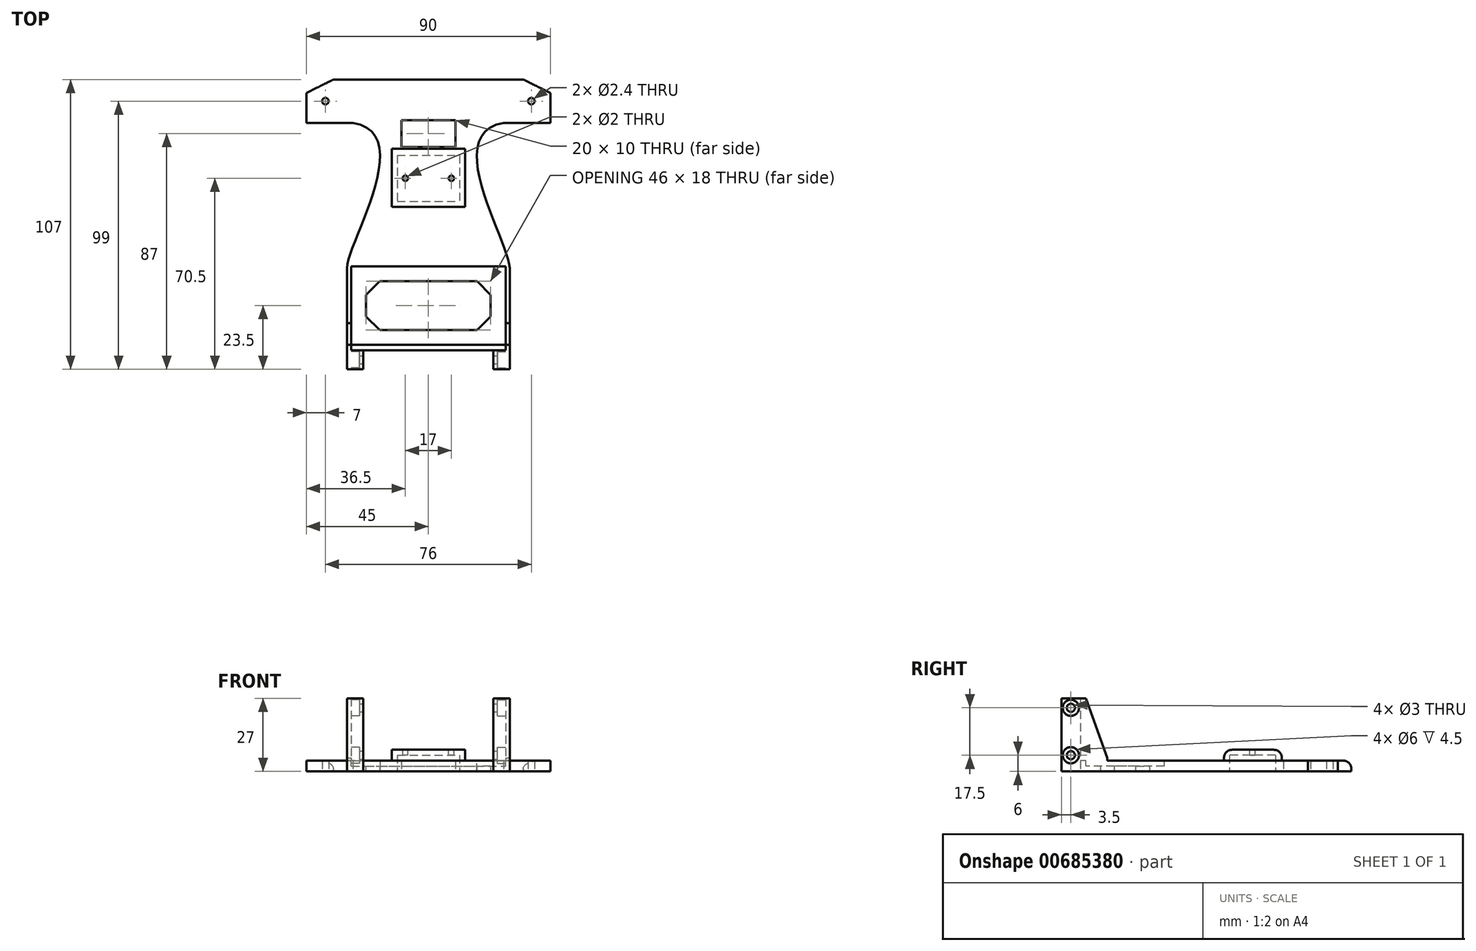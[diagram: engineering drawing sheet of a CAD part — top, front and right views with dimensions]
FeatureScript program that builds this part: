
annotation { "Feature Type Name" : "Feature", "Feature Type Description" : "" }
export const myFeature = defineFeature(function(context is Context, id is Id, definition is map)
    precondition{}
    {
        {
            var Q0;
            Q0=qCreatedBy(makeId("Top.planeOp"),FACE);
            var sketch = newSketch(context, id + "F0", { "sketchPlane" : qUnion([Q0])});
            skLineSegment(sketch, "E0", {"start": v(-45, 84) * mm, "end": v(-45, 68) * mm});
            skLineSegment(sketch, "E1", {"start": v(-45, 68) * mm, "end": v(-30, 68) * mm});
            skLineSegment(sketch, "E2", {"start": v(-30, 14.37) * mm, "end": v(-30, -16) * mm});
            skLineSegment(sketch, "E3", {"start": v(-30, -16) * mm, "end": v(0, -16) * mm});
            skLineSegment(sketch, "E4", {"start": v(-45, 84) * mm, "end": v(0, 84) * mm});
            skLineSegment(sketch, "E5.MirrorCS", {"start": v(45, 84) * mm, "end": v(0, 84) * mm});
            skLineSegment(sketch, "E6.MirrorCS", {"start": v(45, 84) * mm, "end": v(45, 68) * mm});
            skLineSegment(sketch, "E7.MirrorCS", {"start": v(45, 68) * mm, "end": v(30, 68) * mm});
            skLineSegment(sketch, "E8.MirrorCS", {"start": v(30, 14.37) * mm, "end": v(30, -16) * mm});
            skLineSegment(sketch, "E9.MirrorCS", {"start": v(30, -16) * mm, "end": v(0, -16) * mm});
            skCircle(sketch, "E10", {"center": v(-38, 76) * mm, "radius": 1.2 * mm});
            skCircle(sketch, "E11.MirrorC", {"center": v(38, 76) * mm, "radius": 1.2 * mm});
            skLineSegment(sketch, "E12", {"start": v(-30, 68) * mm, "end": v(-27.83, 68) * mm});
            skFitSpline(sketch, "E13", {"points": [v(-27.83, 68) * mm, v(-30, 14.37) * mm], "startDerivative": vector(70.93, -12) * mm, "endDerivative": vector(0, -28.08) * mm});
            skFitSpline(sketch, "E14.MirrorCS", {"points": [v(27.83, 68) * mm, v(30, 14.37) * mm], "startDerivative": vector(-70.93, -12) * mm, "endDerivative": vector(0, -28.08) * mm});
            skLineSegment(sketch, "E15.MirrorCS", {"start": v(30, 68) * mm, "end": v(27.83, 68) * mm});
            skPoint(sketch, "E16.orphan", {"position": v(30, 68) * mm});
            skLineSegment(sketch, "E17.bottom", {"start": v(-10, 69) * mm, "end": v(10, 69) * mm});
            skLineSegment(sketch, "E17.top", {"start": v(-10, 59) * mm, "end": v(10, 59) * mm});
            skLineSegment(sketch, "E17.left", {"start": v(-10, 69) * mm, "end": v(-10, 59) * mm});
            skLineSegment(sketch, "E17.right", {"start": v(10, 69) * mm, "end": v(10, 59) * mm});
            skLineSegment(sketch, "E18.bottom", {"start": v(-23, 9.5) * mm, "end": v(23, 9.5) * mm});
            skLineSegment(sketch, "E18.top", {"start": v(-23, -8.5) * mm, "end": v(23, -8.5) * mm});
            skLineSegment(sketch, "E18.left", {"start": v(-23, 9.5) * mm, "end": v(-23, -8.5) * mm});
            skLineSegment(sketch, "E18.right", {"start": v(23, 9.5) * mm, "end": v(23, -8.5) * mm});
            skPoint(sketch, "E19", {"position": v(-10, 64) * mm});
            skLineSegment(sketch, "E20.bottom", {"start": v(-11.5, 56) * mm, "end": v(11.5, 56) * mm});
            skLineSegment(sketch, "E20.top", {"start": v(-11.5, 39) * mm, "end": v(11.5, 39) * mm});
            skLineSegment(sketch, "E20.left", {"start": v(-11.5, 56) * mm, "end": v(-11.5, 39) * mm});
            skLineSegment(sketch, "E20.right", {"start": v(11.5, 56) * mm, "end": v(11.5, 39) * mm});
            skSolve(sketch);
        }
        {
            var Q0;
            Q0=qSketchRegion(id+"F0",true);
            extrude(context, id + "F1", {"entities" : qUnion([Q0]), "depth" : 4 * mm, "offsetDistance" : 25 * mm});
        }
        {
            var Q0;
            Q0=makeQuery(id+"F1.opExtrude","SWEPT_EDGE",EDGE,{"disambiguationData":[OSD([sQuery(id+"F0.wireOp",EDGE,"E5.MirrorCS"),sQuery(id+"F0.wireOp",EDGE,"E6.MirrorCS")])]});
            chamfer(context, id + "F2", {"entities" : qUnion([Q0]), "chamferType" : ChamferType.TWO_OFFSETS, "width1" : 10 * mm, "oppositeDirection" : false, "width2" : 5 * mm, "tangentPropagation" : true});
        }
        {
            var Q0;
            Q0=makeQuery(id+"F1.opExtrude","SWEPT_EDGE",EDGE,{"disambiguationData":[OSD([sQuery(id+"F0.wireOp",EDGE,"E0"),sQuery(id+"F0.wireOp",EDGE,"E4")])]});
            chamfer(context, id + "F3", {"entities" : qUnion([Q0]), "chamferType" : ChamferType.TWO_OFFSETS, "width1" : 5 * mm, "oppositeDirection" : false, "width2" : 10 * mm, "tangentPropagation" : true});
        }
        {
            var Q0;
            Q0=makeQuery(id+"F1.opExtrude","SWEPT_EDGE",EDGE,{"disambiguationData":[OSD([sQuery(id+"F0.wireOp",EDGE,"E18.bottom"),sQuery(id+"F0.wireOp",EDGE,"E18.left")])]});
            var Q1;
            Q1=makeQuery(id+"F1.opExtrude","SWEPT_EDGE",EDGE,{"disambiguationData":[OSD([sQuery(id+"F0.wireOp",EDGE,"E18.bottom"),sQuery(id+"F0.wireOp",EDGE,"E18.right")])]});
            var Q2;
            Q2=makeQuery(id+"F1.opExtrude","SWEPT_EDGE",EDGE,{"disambiguationData":[OSD([sQuery(id+"F0.wireOp",EDGE,"E18.top"),sQuery(id+"F0.wireOp",EDGE,"E18.right")])]});
            var Q3;
            Q3=makeQuery(id+"F1.opExtrude","SWEPT_EDGE",EDGE,{"disambiguationData":[OSD([sQuery(id+"F0.wireOp",EDGE,"E18.top"),sQuery(id+"F0.wireOp",EDGE,"E18.left")])]});
            chamfer(context, id + "F4", {"entities" : qUnion([Q0, Q1, Q2, Q3]), "width" : 5 * mm, "tangentPropagation" : true});
        }
        {
            var Q0;
            Q0=qCreatedBy(makeId("Top.planeOp"),FACE);
            var sketch = newSketch(context, id + "F5", { "sketchPlane" : qUnion([Q0])});
            skLineSegment(sketch, "E21.bottom", {"start": v(-28.5, -16) * mm, "end": v(-24, -16) * mm});
            skLineSegment(sketch, "E21.top", {"start": v(-30, -23) * mm, "end": v(-24, -23) * mm});
            skLineSegment(sketch, "E21.left", {"start": v(-30, -16) * mm, "end": v(-30, -23) * mm});
            skLineSegment(sketch, "E21.right", {"start": v(-24, -16) * mm, "end": v(-24, -23) * mm});
            skLineSegment(sketch, "E22.MirrorCS", {"start": v(30, -16) * mm, "end": v(30, -23) * mm});
            skLineSegment(sketch, "E23.MirrorCS", {"start": v(30, -16) * mm, "end": v(24, -16) * mm});
            skLineSegment(sketch, "E24.MirrorCS", {"start": v(24, -16) * mm, "end": v(24, -23) * mm});
            skLineSegment(sketch, "E25.MirrorCS", {"start": v(30, -23) * mm, "end": v(24, -23) * mm});
            skLineSegment(sketch, "E26.top", {"start": v(-30, -6) * mm, "end": v(-28.5, -6) * mm});
            skLineSegment(sketch, "E26.left", {"start": v(-30, -16) * mm, "end": v(-30, -6) * mm});
            skLineSegment(sketch, "E26.right", {"start": v(-28.5, -16) * mm, "end": v(-28.5, -6) * mm});
            skLineSegment(sketch, "E27.MirrorCS", {"start": v(30, -16) * mm, "end": v(30, -6) * mm});
            skLineSegment(sketch, "E28.MirrorCS", {"start": v(30, -6) * mm, "end": v(28.5, -6) * mm});
            skLineSegment(sketch, "E29.MirrorCS", {"start": v(28.5, -16) * mm, "end": v(28.5, -6) * mm});
            skSolve(sketch);
        }
        {
            var Q0;
            Q0 = qSketchRegion(id + "F5", true);
            extrude(context, id + "F6", {"entities" : qUnion([Q0]), "operationType" : NewBodyOperationType.ADD, "depth" : 27 * mm, "offsetDistance" : 25 * mm});
        }
        {
            var Q0;
            Q0=makeQuery(id+"F6.boolean.opBoolean","MERGE",FACE,{"derivedFrom":[makeQuery(id+"F1.opExtrude","SWEPT_FACE",FACE,{"disambiguationData":[OSD([sQuery(id+"F0.wireOp",EDGE,"E8.MirrorCS")])]}),makeQuery(id+"F6.opExtrude","SWEPT_FACE",FACE,{"disambiguationData":[OSD([sQuery(id+"F5.wireOp",EDGE,"E22.MirrorCS"),sQuery(id+"F5.wireOp",EDGE,"E27.MirrorCS")])]})]});
            var sketch = newSketch(context, id + "F7", { "sketchPlane" : qUnion([Q0])});
            skCircle(sketch, "E30", {"center": v(-19.5, 23.5) * mm, "radius": 1.5 * mm});
            skCircle(sketch, "E31", {"center": v(-19.5, 6) * mm, "radius": 1.5 * mm});
            skSolve(sketch);
        }
        {
            var Q0;
            Q0 = qSketchRegion(id + "F7", true);
            extrude(context, id + "F8", {"entities" : qUnion([Q0]), "operationType" : NewBodyOperationType.REMOVE, "oppositeDirection" : true, "depth" : 60 * mm, "offsetDistance" : 25 * mm});
        }
        {
            var Q0;
            Q0=makeQuery(id+"F6.boolean.opBoolean","MERGE",FACE,{"derivedFrom":[makeQuery(id+"F1.opExtrude","SWEPT_FACE",FACE,{"disambiguationData":[OSD([sQuery(id+"F0.wireOp",EDGE,"E8.MirrorCS")])]}),makeQuery(id+"F6.opExtrude","SWEPT_FACE",FACE,{"disambiguationData":[OSD([sQuery(id+"F5.wireOp",EDGE,"E22.MirrorCS"),sQuery(id+"F5.wireOp",EDGE,"E27.MirrorCS")])]})]});
            var sketch = newSketch(context, id + "F9", { "sketchPlane" : qUnion([Q0])});
            skCircle(sketch, "E32", {"center": v(-19.5, 23.5) * mm, "radius": 3 * mm});
            skCircle(sketch, "E33", {"center": v(-19.5, 6) * mm, "radius": 3 * mm});
            skSolve(sketch);
        }
        {
            var Q0;
            Q0 = qSketchRegion(id + "F9", true);
            extrude(context, id + "F10", {"entities" : qUnion([Q0]), "operationType" : NewBodyOperationType.REMOVE, "oppositeDirection" : true, "depth" : 4.5 * mm, "offsetDistance" : 25 * mm});
        }
        {
            var Q0;
            Q0=makeQuery(id+"F6.boolean.opBoolean","MERGE",FACE,{"derivedFrom":[makeQuery(id+"F1.opExtrude","SWEPT_FACE",FACE,{"disambiguationData":[OSD([sQuery(id+"F0.wireOp",EDGE,"E2")])]}),makeQuery(id+"F6.opExtrude","SWEPT_FACE",FACE,{"disambiguationData":[OSD([sQuery(id+"F5.wireOp",EDGE,"E21.left"),sQuery(id+"F5.wireOp",EDGE,"E26.left")])]})]});
            var sketch = newSketch(context, id + "F11", { "sketchPlane" : qUnion([Q0])});
            skCircle(sketch, "E34", {"center": v(19.5, 23.5) * mm, "radius": 3 * mm});
            skCircle(sketch, "E35", {"center": v(19.5, 6) * mm, "radius": 3 * mm});
            skSolve(sketch);
        }
        {
            var Q0;
            Q0 = qSketchRegion(id + "F11", true);
            extrude(context, id + "F12", {"entities" : qUnion([Q0]), "operationType" : NewBodyOperationType.REMOVE, "oppositeDirection" : true, "depth" : 4.5 * mm, "offsetDistance" : 25 * mm});
        }
        {
            var Q0;
            Q0=makeQuery(id+"F1.opExtrude","CAP_FACE",FACE,{"disambiguationData":[OSD([sQuery(id+"F0.wireOp",EDGE,"E0"),sQuery(id+"F0.wireOp",EDGE,"E1"),sQuery(id+"F0.wireOp",EDGE,"E2"),sQuery(id+"F0.wireOp",EDGE,"E3"),sQuery(id+"F0.wireOp",EDGE,"E4"),sQuery(id+"F0.wireOp",EDGE,"E5.MirrorCS"),sQuery(id+"F0.wireOp",EDGE,"E6.MirrorCS"),sQuery(id+"F0.wireOp",EDGE,"E7.MirrorCS"),sQuery(id+"F0.wireOp",EDGE,"E8.MirrorCS"),sQuery(id+"F0.wireOp",EDGE,"E9.MirrorCS"),sQuery(id+"F0.wireOp",EDGE,"U4RAMHwO-AoFx-lwUL-oOQ6-DCnqhpArdnzn"),sQuery(id+"F0.wireOp",EDGE,"E10"),sQuery(id+"F0.wireOp",EDGE,"24563574-8a27-4f83-a6c0-6041d10e9e610.MirrorC"),sQuery(id+"F0.wireOp",EDGE,"E11.MirrorC"),sQuery(id+"F0.wireOp",EDGE,"E12"),sQuery(id+"F0.wireOp",EDGE,"E13"),sQuery(id+"F0.wireOp",EDGE,"E14.MirrorCS"),sQuery(id+"F0.wireOp",EDGE,"E15.MirrorCS"),sQuery(id+"F0.wireOp",EDGE,"E17.bottom"),sQuery(id+"F0.wireOp",EDGE,"E17.top"),sQuery(id+"F0.wireOp",EDGE,"E17.left"),sQuery(id+"F0.wireOp",EDGE,"E17.right"),sQuery(id+"F0.wireOp",EDGE,"E18.bottom"),sQuery(id+"F0.wireOp",EDGE,"E18.top"),sQuery(id+"F0.wireOp",EDGE,"E18.left"),sQuery(id+"F0.wireOp",EDGE,"E18.right"),sQuery(id+"F0.wireOp",EDGE,"iSs1wg75-Nd3i-FdQh-0eUU-iPC7muo31p7i")])],"isStart":false});
            var sketch = newSketch(context, id + "F13", { "sketchPlane" : qUnion([Q0])});
            skLineSegment(sketch, "E36.bottom", {"start": v(-28.5, 15) * mm, "end": v(28.5, 15) * mm});
            skLineSegment(sketch, "E36.top", {"start": v(-28.5, -14) * mm, "end": v(28.5, -14) * mm});
            skLineSegment(sketch, "E36.left", {"start": v(-28.5, 15) * mm, "end": v(-28.5, -14) * mm});
            skLineSegment(sketch, "E36.right", {"start": v(28.5, 15) * mm, "end": v(28.5, -14) * mm});
            skSolve(sketch);
        }
        {
            var Q0;
            Q0 = qSketchRegion(id + "F13", true);
            extrude(context, id + "F14", {"entities" : qUnion([Q0]), "operationType" : NewBodyOperationType.REMOVE, "oppositeDirection" : true, "depth" : 2 * mm, "offsetDistance" : 25 * mm});
        }
        {
            var Q0;
            Q0=makeQuery(id+"F6.opExtrude","CAP_EDGE",EDGE,{"disambiguationData":[OSD([sQuery(id+"F5.wireOp",EDGE,"E28.MirrorCS")])],"isStart":false});
            chamfer(context, id + "F15", {"entities" : qUnion([Q0]), "chamferType" : ChamferType.TWO_OFFSETS, "width1" : 8 * mm, "oppositeDirection" : false, "width2" : 22 * mm, "tangentPropagation" : true});
        }
        {
            var Q0;
            Q0=makeQuery(id+"F6.opExtrude","CAP_EDGE",EDGE,{"disambiguationData":[OSD([sQuery(id+"F5.wireOp",EDGE,"E26.top")])],"isStart":false});
            chamfer(context, id + "F16", {"entities" : qUnion([Q0]), "chamferType" : ChamferType.TWO_OFFSETS, "width1" : 22 * mm, "oppositeDirection" : false, "width2" : 8 * mm, "tangentPropagation" : true});
        }
        {
            var Q0;
            {var subQ0=sQuery(id+"F0.wireOp",EDGE,"E4");var subQ1=sQuery(id+"F0.wireOp",EDGE,"E0");var subQ2=sQuery(id+"F0.wireOp",EDGE,"E12");var subQ3=sQuery(id+"F0.wireOp",EDGE,"E1");var subQ4=sQuery(id+"F0.wireOp",EDGE,"E20.right");var subQ5=sQuery(id+"F0.wireOp",EDGE,"E6.MirrorCS");var subQ6=sQuery(id+"F0.wireOp",EDGE,"E5.MirrorCS");var subQ7=sQuery(id+"F0.wireOp",EDGE,"E20.left");var subQ8=sQuery(id+"F0.wireOp",EDGE,"E20.bottom");var subQ9=sQuery(id+"F0.wireOp",EDGE,"E17.right");var subQ10=sQuery(id+"F0.wireOp",EDGE,"E17.left");var subQ11=sQuery(id+"F0.wireOp",EDGE,"E17.top");var subQ12=sQuery(id+"F0.wireOp",EDGE,"E17.bottom");var subQ13=sQuery(id+"F0.wireOp",EDGE,"E14.MirrorCS");var subQ14=sQuery(id+"F0.wireOp",EDGE,"E2");var subQ15=sQuery(id+"F0.wireOp",EDGE,"E20.top");var subQ16=sQuery(id+"F0.wireOp",EDGE,"E11.MirrorC");var subQ17=sQuery(id+"F0.wireOp",EDGE,"E15.MirrorCS");var subQ18=sQuery(id+"F0.wireOp",EDGE,"E7.MirrorCS");var subQ19=sQuery(id+"F0.wireOp",EDGE,"E8.MirrorCS");var subQ20=sQuery(id+"F0.wireOp",EDGE,"E10");var subQ21=sQuery(id+"F0.wireOp",EDGE,"E13");Q0=makeQuery(id+"F14.boolean.opBoolean","SPLIT",FACE,{"disambiguationData":[TD([makeQuery(id+"F1.opExtrude","SWEPT_FACE",FACE,{"disambiguationData":[OSD([subQ1])]})])],"derivedFrom":makeQuery(id+"F1.opExtrude","CAP_FACE",FACE,{"disambiguationData":[OSD([subQ1,subQ3,subQ14,sQuery(id+"F0.wireOp",EDGE,"E3"),subQ0,subQ6,subQ5,subQ18,subQ19,sQuery(id+"F0.wireOp",EDGE,"E9.MirrorCS"),subQ20,subQ16,subQ2,subQ21,subQ13,subQ17,subQ12,subQ11,subQ10,subQ9,sQuery(id+"F0.wireOp",EDGE,"E18.bottom"),sQuery(id+"F0.wireOp",EDGE,"E18.top"),sQuery(id+"F0.wireOp",EDGE,"E18.left"),sQuery(id+"F0.wireOp",EDGE,"E18.right"),subQ8,subQ15,subQ7,subQ4])],"isStart":false})});}
            var sketch = newSketch(context, id + "F17", { "sketchPlane" : qUnion([Q0])});
            skLineSegment(sketch, "E37.bottom", {"start": v(-11.5, 56) * mm, "end": v(11.5, 56) * mm});
            skLineSegment(sketch, "E37.top", {"start": v(-11.5, 39) * mm, "end": v(11.5, 39) * mm});
            skLineSegment(sketch, "E37.left", {"start": v(-11.5, 56) * mm, "end": v(-11.5, 39) * mm});
            skLineSegment(sketch, "E37.right", {"start": v(11.5, 56) * mm, "end": v(11.5, 39) * mm});
            skLineSegment(sketch, "E38.bottom", {"start": v(-13.5, 58.38) * mm, "end": v(13.5, 58.38) * mm});
            skLineSegment(sketch, "E38.top", {"start": v(-13.5, 37) * mm, "end": v(13.5, 37) * mm});
            skLineSegment(sketch, "E38.left", {"start": v(-13.5, 58.38) * mm, "end": v(-13.5, 37) * mm});
            skLineSegment(sketch, "E38.right", {"start": v(13.5, 58.38) * mm, "end": v(13.5, 37) * mm});
            skSolve(sketch);
        }
        {
            var Q0;
            Q0 = qSketchRegion(id + "F17", true);
            extrude(context, id + "F18", {"entities" : qUnion([Q0]), "operationType" : NewBodyOperationType.ADD, "depth" : 2 * mm, "offsetDistance" : 25 * mm});
        }
        {
            var Q0;
            Q0=makeQuery(id+"F18.opExtrude","CAP_FACE",FACE,{"disambiguationData":[OSD([sQuery(id+"F17.wireOp",EDGE,"E37.bottom"),sQuery(id+"F17.wireOp",EDGE,"E37.top"),sQuery(id+"F17.wireOp",EDGE,"E37.left"),sQuery(id+"F17.wireOp",EDGE,"E37.right"),sQuery(id+"F17.wireOp",EDGE,"E38.bottom"),sQuery(id+"F17.wireOp",EDGE,"E38.top"),sQuery(id+"F17.wireOp",EDGE,"E38.left"),sQuery(id+"F17.wireOp",EDGE,"E38.right")])],"isStart":false});
            var sketch = newSketch(context, id + "F19", { "sketchPlane" : qUnion([Q0])});
            skLineSegment(sketch, "E39.bottom", {"start": v(-13.5, 58.38) * mm, "end": v(13.5, 58.38) * mm});
            skLineSegment(sketch, "E39.top", {"start": v(-13.5, 37) * mm, "end": v(13.5, 37) * mm});
            skLineSegment(sketch, "E39.left", {"start": v(-13.5, 58.38) * mm, "end": v(-13.5, 37) * mm});
            skLineSegment(sketch, "E39.right", {"start": v(13.5, 58.38) * mm, "end": v(13.5, 37) * mm});
            skSolve(sketch);
        }
        {
            var Q0;
            Q0 = qSketchRegion(id + "F19", true);
            extrude(context, id + "F20", {"entities" : qUnion([Q0]), "operationType" : NewBodyOperationType.ADD, "depth" : 2 * mm, "offsetDistance" : 25 * mm});
        }
        {
            var Q0;
            Q0=makeQuery(id+"F20.opExtrude","CAP_FACE",FACE,{"disambiguationData":[OSD([sQuery(id+"F19.wireOp",EDGE,"E39.bottom"),sQuery(id+"F19.wireOp",EDGE,"E39.top"),sQuery(id+"F19.wireOp",EDGE,"E39.left"),sQuery(id+"F19.wireOp",EDGE,"E39.right")])],"isStart":false});
            var sketch = newSketch(context, id + "F21", { "sketchPlane" : qUnion([Q0])});
            skCircle(sketch, "E40", {"center": v(-8.5, 47.5) * mm, "radius": 1 * mm});
            skCircle(sketch, "E41", {"center": v(8.5, 47.5) * mm, "radius": 1 * mm});
            skSolve(sketch);
        }
        {
            var Q0;
            Q0 = qSketchRegion(id + "F21", true);
            extrude(context, id + "F22", {"entities" : qUnion([Q0]), "operationType" : NewBodyOperationType.REMOVE, "oppositeDirection" : true, "depth" : 2 * mm, "offsetDistance" : 25 * mm});
        }
        {
            var Q0;
            Q0=makeQuery(id+"F20.opExtrude","CAP_EDGE",EDGE,{"disambiguationData":[OSD([sQuery(id+"F19.wireOp",EDGE,"E39.bottom")])],"isStart":false});
            var Q1;
            Q1=makeQuery(id+"F1.opExtrude","CAP_EDGE",EDGE,{"disambiguationData":[OSD([sQuery(id+"F0.wireOp",EDGE,"E4"),sQuery(id+"F0.wireOp",EDGE,"E5.MirrorCS")])],"isStart":false});
            var Q2;
            Q2=makeQuery(id+"F20.opExtrude","CAP_EDGE",EDGE,{"disambiguationData":[OSD([sQuery(id+"F19.wireOp",EDGE,"E39.top")])],"isStart":false});
            fillet(context, id + "F23", {"entities" : qUnion([Q0, Q1, Q2]), "tangentPropagation" : true, "radius" : 3 * mm, "defaultsChanged" : false, "vertexSettings" : [], "allowEdgeOverflow" : false});
        }
    });
